# Revit family: Haworth_CabanaLounge_CollaborativeSofa_Armless
name_source: partatom
category: Furniture
revit_build: Autodesk Revit 2018 (Build: 20170223_1515(x64)
units: mm (PartAtom-declared; Revit-internal decimal feet)

## family parameters
Always vertical = Yes
Cut with Voids When Loaded = No
OmniClass Number = 23.40.70.14.64.21
OmniClass Title = Systems Furniture
Room Calculation Point = No
Shared = No
Work Plane-Based = No

## types (7) — shared parameters
Actual Depth = 30"
Actual Height = 30 3/8"
Assembly Code = E2020200
Leg Offset = 2 3/4"
Manufacturer = Haworth
Model = Haworth Cabana
Revision Number = 1
Seat Height = 18 1/16"
Size = Verify Final Dim. w/ Haworth
URL = http://www.haworth.com
URL - Product = https://www.haworth.com
Warranty = http://www.haworth.com

## per-type parameters (varying)
| type | 2S HalfBack | Actual Width | Back Control | Back Width | Description | Full Back | Half Back | Integrated Table Control | No Back | One Seat | Two Seats | With Top |
| S9CB-0 - Two Seats - Full Back - With Integrated Table | No | 72" | Yes | 72" | Haworth Cabana Collaborative Sofa - Two Seats - Armless - Full Back - With Integrated Table | Yes | No | Yes | No | No | Yes | Yes |
| S9CH-0 - Two Seats - Half Back - With Integrated Table | Yes | 72" | Yes | 42" | Haworth Cabana Collaborative Sofa - Two Seats - Armless - Half Back - With Integrated Table | No | Yes | Yes | No | No | Yes | Yes |
| S9CH-0 - Two Seats - Half Back - Without Integrated Table | Yes | 72" | Yes | 42" | Haworth Cabana Collaborative Sofa - Two Seats - Armless - Half Back - Without Integrated Table | No | Yes | No | No | No | Yes | No |
| S9CB-0 - Two Seats - Full Back - Without Integrated Table | No | 72" | Yes | 72" | Haworth Cabana Collaborative Sofa - Two Seats - Armless - Full Back - Without Integrated Table | Yes | No | No | No | No | Yes | No |
| S9C0-0 - Two Seats - No Back - Without Integrated Table | No | 72" | No | 72" | Haworth Cabana Collaborative Sofa - Two Seats - Armless - No Back - Without Integrated Table | No | No | No | Yes | No | Yes | No |
| S9B0-0 - One Seat - No Back - Without Integrated Table | No | 36" | No | 36" | Haworth Cabana Collaborative Sofa - One Seat - Armless - No Back - Without Integrated Table | No | No | No | Yes | Yes | No | No |
| S9BB-0 - One Seat - Full Back - Without Integrated Table | No | 36" | Yes | 36" | Haworth Cabana Collaborative Sofa - One Seat - Armless - Full Back - Without Integrated Table | Yes | No | No | No | Yes | No | No |

## geometry (parser evidence)
native form markers: Extrusion x3, Sweep x8
no freeform markers — native parametric forms only
